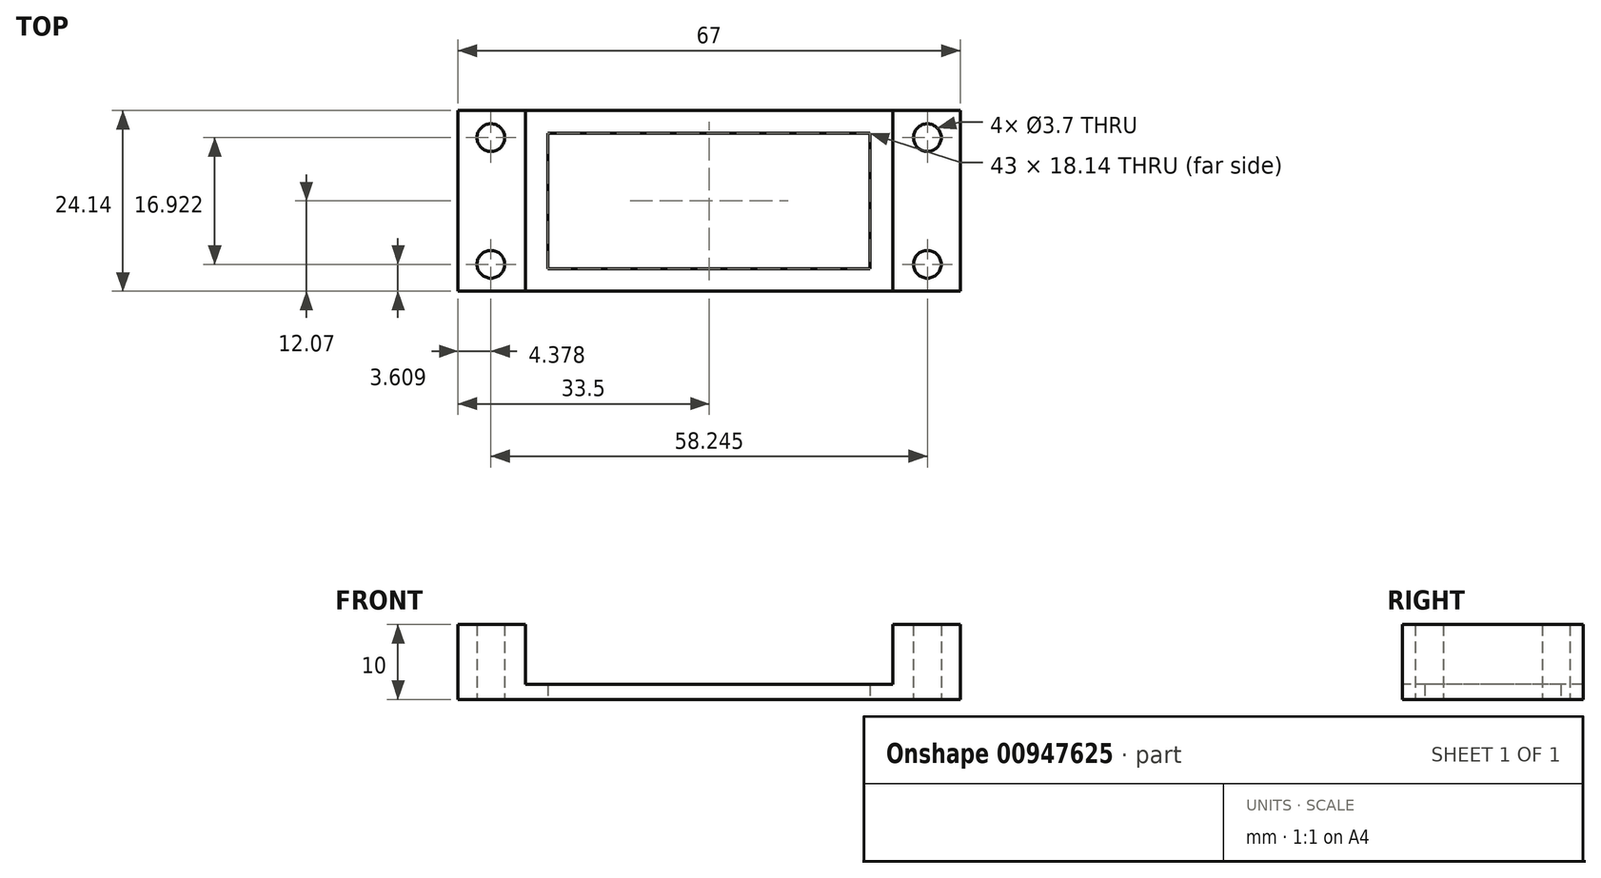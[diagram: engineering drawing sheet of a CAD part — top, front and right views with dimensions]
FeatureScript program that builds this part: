
annotation { "Feature Type Name" : "Feature", "Feature Type Description" : "" }
export const myFeature = defineFeature(function(context is Context, id is Id, definition is map)
    precondition{}
    {
        {
            var Q0;
            Q0=qCreatedBy(makeId("Top.planeOp"),FACE);
            var sketch = newSketch(context, id + "F0", { "sketchPlane" : qUnion([Q0])});
            skLineSegment(sketch, "E0.bottom", {"start": v(0, 0) * mm, "end": v(-21.5, 0) * mm});
            skLineSegment(sketch, "E0.top", {"start": v(0, -9.07) * mm, "end": v(-21.5, -9.07) * mm});
            skLineSegment(sketch, "E0.left", {"start": v(0, 0) * mm, "end": v(0, -9.07) * mm});
            skLineSegment(sketch, "E0.right", {"start": v(-21.5, 0) * mm, "end": v(-21.5, -9.07) * mm});
            skLineSegment(sketch, "E1.bottom", {"start": v(0, 0) * mm, "end": v(-33.5, 0) * mm});
            skLineSegment(sketch, "E1.top", {"start": v(0, -12.07) * mm, "end": v(-33.5, -12.07) * mm});
            skLineSegment(sketch, "E1.left", {"start": v(0, 0) * mm, "end": v(0, -12.07) * mm});
            skLineSegment(sketch, "E1.right", {"start": v(-33.5, 0) * mm, "end": v(-33.5, -12.07) * mm});
            skCircle(sketch, "E2", {"center": v(-29.12, -8.46) * mm, "radius": 1.85 * mm});
            skLineSegment(sketch, "E3.bottom", {"start": v(-33.5, 0) * mm, "end": v(-24.5, 0) * mm});
            skLineSegment(sketch, "E3.top", {"start": v(-33.5, -12.07) * mm, "end": v(-24.5, -12.07) * mm});
            skLineSegment(sketch, "E3.right", {"start": v(-24.5, 0) * mm, "end": v(-24.5, -12.07) * mm});
            skSolve(sketch);
        }
        {
            var Q0;
            Q0=makeQuery(id+"F0.imprint","IMPRINT",FACE,{"disambiguationData":[TD([[makeQuery(id+"F0.imprint","IMPRINT",EDGE,{"derivedFrom":sQuery(id+"F0.wireOp",EDGE,"E0.top")}),1.0]])]});
            extrude(context, id + "F1", {"entities" : qUnion([Q0]), "depth" : 2 * mm, "offsetDistance" : 25 * mm});
        }
        {
            var Q0;
            {var subQ0=sQuery(id+"F0.wireOp",EDGE,"E1.right");Q0=makeQuery(id+"F0.imprint","IMPRINT",FACE,{"disambiguationData":[TD([[makeQuery(id+"F0.imprint","IMPRINT",EDGE,{"derivedFrom":subQ0}),1.0]])]});}
            extrude(context, id + "F2", {"entities" : qUnion([Q0]), "operationType" : NewBodyOperationType.ADD, "depth" : 10 * mm, "offsetDistance" : 25 * mm});
        }
        {
            var Q0;
            Q0=makeQuery(id+"F1.opExtrude","SWEPT_BODY",BODY,{"disambiguationData":[OSD([sQuery(id+"F0.wireOp",EDGE,"E0.top"),sQuery(id+"F0.wireOp",EDGE,"E0.right"),sQuery(id+"F0.wireOp",EDGE,"E1.bottom"),sQuery(id+"F0.wireOp",EDGE,"E1.top"),sQuery(id+"F0.wireOp",EDGE,"E1.left"),sQuery(id+"F0.wireOp",EDGE,"E3.right")])]});
            var Q1;
            {var subQ0=sQuery(id+"F0.wireOp",EDGE,"E1.bottom");Q1=makeQuery(id+"F2.boolean.opBoolean","MERGE",FACE,{"derivedFrom":[makeQuery(id+"F1.opExtrude","SWEPT_FACE",FACE,{"disambiguationData":[OSD([subQ0])]}),makeQuery(id+"F2.opExtrude","SWEPT_FACE",FACE,{"disambiguationData":[OSD([subQ0])]})]});}
            mirror(context, id + "F3", {"operationType" : NewBodyOperationType.ADD, "entities" : qUnion([Q0]), "mirrorPlane" : qUnion([Q1])});
        }
        {
            var Q0;
            Q0=makeQuery(id+"F1.opExtrude","SWEPT_BODY",BODY,{"disambiguationData":[OSD([sQuery(id+"F0.wireOp",EDGE,"E0.top"),sQuery(id+"F0.wireOp",EDGE,"E0.right"),sQuery(id+"F0.wireOp",EDGE,"E1.bottom"),sQuery(id+"F0.wireOp",EDGE,"E1.top"),sQuery(id+"F0.wireOp",EDGE,"E1.left"),sQuery(id+"F0.wireOp",EDGE,"E3.right")])]});
            var Q1;
            Q1=qCreatedBy(makeId("Right.planeOp"),FACE);
            mirror(context, id + "F4", {"operationType" : NewBodyOperationType.ADD, "entities" : qUnion([Q0]), "mirrorPlane" : qUnion([Q1])});
        }
    });
